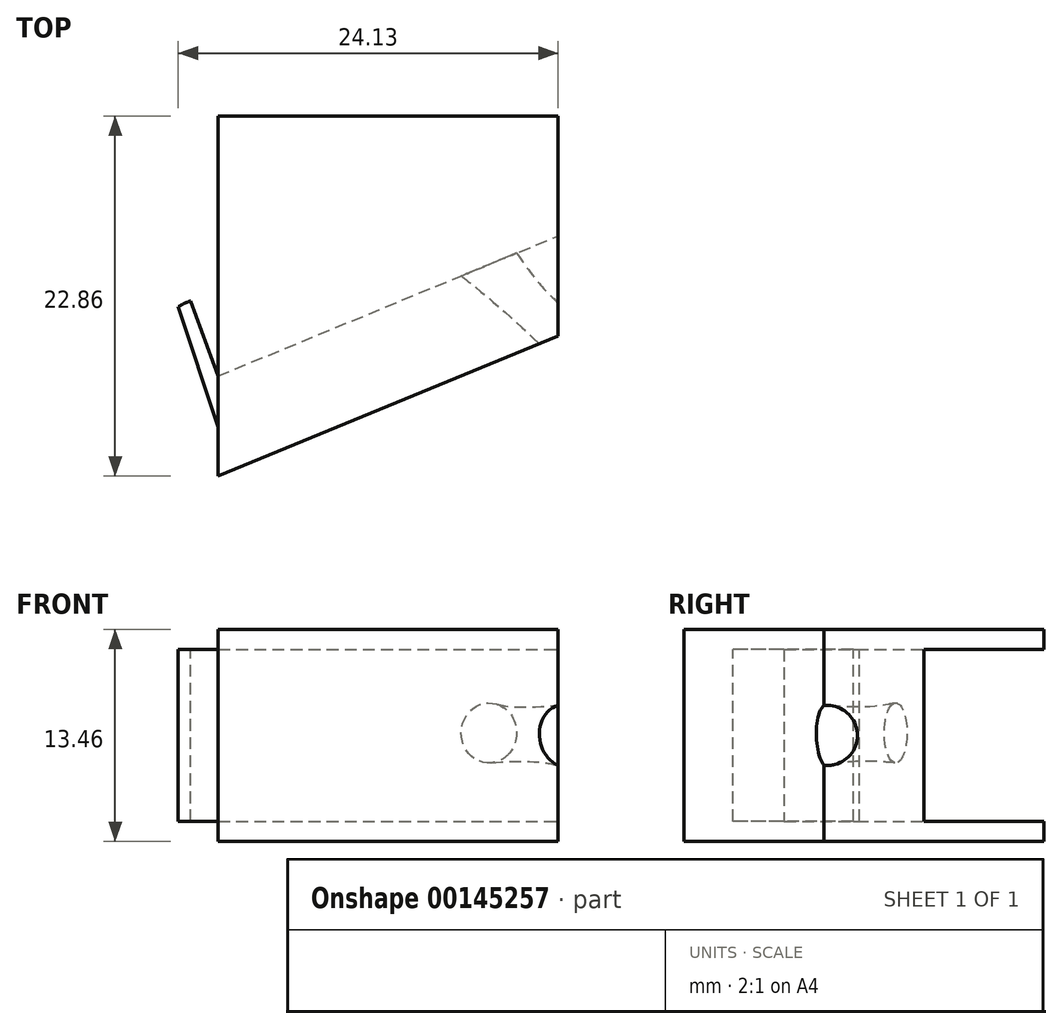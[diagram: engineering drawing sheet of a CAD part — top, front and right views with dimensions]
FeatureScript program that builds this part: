
annotation { "Feature Type Name" : "Feature", "Feature Type Description" : "" }
export const myFeature = defineFeature(function(context is Context, id is Id, definition is map)
    precondition{}
    {
        {
            var Q0;
            Q0=qCreatedBy(makeId("Top.planeOp"),FACE);
            var sketch = newSketch(context, id + "F0", { "sketchPlane" : qUnion([Q0])});
            skLineSegment(sketch, "E0.top", {"start": v(1.27, 3.85) * mm, "end": v(12.07, 3.85) * mm});
            skLineSegment(sketch, "E0.right", {"start": v(12.07, -0.48) * mm, "end": v(12.07, 3.85) * mm});
            skLineSegment(sketch, "E1.top", {"start": v(12.07, -2.5) * mm, "end": v(-9.52, -2.5) * mm});
            skLineSegment(sketch, "E1.left", {"start": v(12.07, 3.85) * mm, "end": v(12.07, -2.5) * mm});
            skLineSegment(sketch, "E1.right", {"start": v(-9.52, 3.85) * mm, "end": v(-9.52, -2.5) * mm});
            skLineSegment(sketch, "E2", {"start": v(-9.52, 3.85) * mm, "end": v(1.27, 3.85) * mm});
            skLineSegment(sketch, "E3", {"start": v(-9.52, 3.85) * mm, "end": v(12.06, 12.74) * mm});
            skLineSegment(sketch, "E4", {"start": v(12.07, 12.74) * mm, "end": v(12.07, 3.85) * mm});
            skLineSegment(sketch, "E5", {"start": v(-9.52, -2.5) * mm, "end": v(12.07, 6.4) * mm});
            skLineSegment(sketch, "E6.top", {"start": v(12.07, 20.36) * mm, "end": v(-9.52, 20.36) * mm});
            skLineSegment(sketch, "E6.left", {"start": v(12.07, -2.5) * mm, "end": v(12.07, 20.36) * mm});
            skLineSegment(sketch, "E6.right", {"start": v(-9.52, -2.5) * mm, "end": v(-9.52, 20.36) * mm});
            skSolve(sketch);
        }
        {
            var Q0;
            {var subQ6=sQuery(id+"F0.wireOp",EDGE,"E2");Q0=makeQuery(id+"F0.imprint","IMPRINT",FACE,{"disambiguationData":[TD([[makeQuery(id+"F0.imprint","IMPRINT",EDGE,{"derivedFrom":subQ6}),1.0]])]});}
            var Q1;
            {var subQ0=sQuery(id+"F0.wireOp",EDGE,"E6.left");var subQ1=sQuery(id+"F0.wireOp",EDGE,"E0.top");var subQ2=makeQuery(id+"F0.imprint","INTERSECT",VERTEX,{"derivedFrom":[subQ1,subQ0]});Q1=makeQuery(id+"F0.imprint","IMPRINT",FACE,{"disambiguationData":[TD([[makeQuery(id+"F0.imprint","IMPRINT",EDGE,{"disambiguationData":[TD([[subQ2,1.0]])],"derivedFrom":subQ1}),1.0]])]});}
            var Q2;
            {var subQ5=sQuery(id+"F0.wireOp",EDGE,"E1.top");Q2=makeQuery(id+"F0.imprint","IMPRINT",FACE,{"disambiguationData":[TD([[makeQuery(id+"F0.imprint","IMPRINT",EDGE,{"derivedFrom":subQ5}),-1.0]])]});}
            var Q3;
            {var subQ0=sQuery(id+"F0.wireOp",EDGE,"E2");Q3=makeQuery(id+"F0.imprint","IMPRINT",FACE,{"disambiguationData":[TD([[makeQuery(id+"F0.imprint","IMPRINT",EDGE,{"derivedFrom":subQ0}),-1.0]])]});}
            extrude(context, id + "F1", {"entities" : qUnion([Q0, Q1, Q2, Q3]), "depth" : 13.46 * mm});
        }
        {
            var Q0;
            Q0=makeQuery(id+"F1.opExtrude","CAP_FACE",FACE,{"disambiguationData":[OSD([sQuery(id+"F0.wireOp",EDGE,"E1.top"),sQuery(id+"F0.wireOp",EDGE,"E1.left"),sQuery(id+"F0.wireOp",EDGE,"E1.right"),sQuery(id+"F0.wireOp",EDGE,"E3"),sQuery(id+"F0.wireOp",EDGE,"E4")])],"isStart":false});
            var sketch = newSketch(context, id + "F2", { "sketchPlane" : qUnion([Q0])});
            skLineSegment(sketch, "E7.bottom", {"start": v(-9.53, -2.5) * mm, "end": v(12.07, -2.5) * mm});
            skLineSegment(sketch, "E7.top", {"start": v(-9.53, 20.36) * mm, "end": v(12.07, 20.36) * mm});
            skLineSegment(sketch, "E7.left", {"start": v(-9.53, -2.5) * mm, "end": v(-9.53, 20.36) * mm});
            skLineSegment(sketch, "E7.right", {"start": v(12.07, -2.5) * mm, "end": v(12.07, 20.36) * mm});
            skSolve(sketch);
        }
        {
            var Q0;
            {var subQ0=sQuery(id+"F2.wireOp",EDGE,"E7.top");Q0=makeQuery(id+"F2.imprint","IMPRINT",FACE,{"disambiguationData":[TD([[makeQuery(id+"F2.imprint","IMPRINT",EDGE,{"derivedFrom":subQ0}),-1.0]])]});}
            extrude(context, id + "F3", {"entities" : qUnion([Q0]), "operationType" : NewBodyOperationType.ADD, "oppositeDirection" : true, "depth" : 1.27 * mm});
        }
        {
            var Q0;
            {var subQ0=sQuery(id+"F0.wireOp",EDGE,"E3");Q0=makeQuery(id+"F0.imprint","IMPRINT",FACE,{"disambiguationData":[TD([[makeQuery(id+"F0.imprint","IMPRINT",EDGE,{"derivedFrom":subQ0}),1.0]])]});}
            extrude(context, id + "F4", {"entities" : qUnion([Q0]), "operationType" : NewBodyOperationType.ADD, "depth" : 1.27 * mm});
        }
        {
            var Q0;
            {var subQ0=sQuery(id+"F0.wireOp",EDGE,"E6.right");Q0=makeQuery(id+"F4.boolean.opBoolean","MERGE",FACE,{"derivedFrom":[makeQuery(id+"F3.boolean.opBoolean","MERGE",FACE,{"derivedFrom":[makeQuery(id+"F1.opExtrude","SWEPT_FACE",FACE,{"disambiguationData":[OSD([subQ0])]}),makeQuery(id+"F3.opExtrude","SWEPT_FACE",FACE,{"disambiguationData":[OSD([sQuery(id+"F2.wireOp",EDGE,"E7.left")])]})]}),makeQuery(id+"F4.opExtrude","SWEPT_FACE",FACE,{"disambiguationData":[OSD([subQ0])]})]});}
            var sketch = newSketch(context, id + "F5", { "sketchPlane" : qUnion([Q0])});
            skPoint(sketch, "E8.oppositeSnap0", {"position": v(-8.93, 13.46) * mm});
            skLineSegment(sketch, "E8.bottom", {"start": v(-3.85, 1.27) * mm, "end": v(-8.93, 1.27) * mm});
            skLineSegment(sketch, "E8.top", {"start": v(-3.85, 12.2) * mm, "end": v(-8.93, 12.2) * mm});
            skLineSegment(sketch, "E8.left", {"start": v(-3.85, 1.27) * mm, "end": v(-3.85, 12.2) * mm});
            skLineSegment(sketch, "E8.right", {"start": v(-8.93, 1.27) * mm, "end": v(-8.93, 12.2) * mm});
            skLineSegment(sketch, "E9.bottom", {"start": v(-2.45, 1.27) * mm, "end": v(-0.6, 1.27) * mm});
            skLineSegment(sketch, "E9.top", {"start": v(-2.45, 12.2) * mm, "end": v(-0.6, 12.2) * mm});
            skLineSegment(sketch, "E9.left", {"start": v(-2.45, 1.27) * mm, "end": v(-2.45, 12.2) * mm});
            skLineSegment(sketch, "E9.right", {"start": v(-0.6, 1.27) * mm, "end": v(-0.6, 12.2) * mm});
            skSolve(sketch);
        }
        {
            var Q0;
            Q0=makeQuery(id+"F5.imprint","IMPRINT",FACE,{"disambiguationData":[TD([[makeQuery(id+"F5.imprint","IMPRINT",EDGE,{"derivedFrom":sQuery(id+"F5.wireOp",EDGE,"E8.bottom")}),-1.0]])]});
            var Q1;
            Q1=sQuery(id+"F5.wireOp",EDGE,"E8.left");
            revolve(context, id + "F6", {"entities" : qUnion([Q0]), "axis" : qUnion([Q1]), "revolveType" : RevolveType.ONE_DIRECTION, "angle" : 30 * degree});
        }
        {
            var Q0;
            Q0=makeQuery(id+"F5.imprint","IMPRINT",FACE,{"disambiguationData":[TD([[makeQuery(id+"F5.imprint","IMPRINT",EDGE,{"derivedFrom":sQuery(id+"F5.wireOp",EDGE,"E8.bottom")}),-1.0]])]});
            var Q1;
            Q1=sQuery(id+"F5.wireOp",EDGE,"E8.left");
            revolve(context, id + "F7", {"operationType" : NewBodyOperationType.REMOVE, "entities" : qUnion([Q0]), "axis" : qUnion([Q1]), "revolveType" : RevolveType.ONE_DIRECTION, "angle" : 20 * degree});
        }
        {
            var Q0;
            Q0=makeQuery(id+"F6.opRevolve","CAP_FACE",FACE,{"disambiguationData":[OSD([sQuery(id+"F5.wireOp",EDGE,"E8.bottom"),sQuery(id+"F5.wireOp",EDGE,"E8.top"),sQuery(id+"F5.wireOp",EDGE,"E8.left"),sQuery(id+"F5.wireOp",EDGE,"E8.right")])],"isStart":false});
            var Q1;
            Q1=makeQuery(id+"F5.imprint","IMPRINT",FACE,{"disambiguationData":[TD([[makeQuery(id+"F5.imprint","IMPRINT",EDGE,{"derivedFrom":sQuery(id+"F5.wireOp",EDGE,"E9.bottom")}),1.0]])]});
            loft(context, id + "F8", {"operationType" : NewBodyOperationType.ADD, "sheetProfilesArray" : [{ "sheetProfileEntities" : qUnion([Q0]) }, { "sheetProfileEntities" : qUnion([Q1]) }]});
        }
        {
            var Q0;
            Q0=makeQuery(id+"F1.opExtrude","SWEPT_FACE",FACE,{"disambiguationData":[OSD([sQuery(id+"F0.wireOp",EDGE,"E3")])]});
            var sketch = newSketch(context, id + "F9", { "sketchPlane" : qUnion([Q0])});
            skCircle(sketch, "E10", {"center": v(-11.26, 6.89) * mm, "radius": 1.9 * mm});
            skSolve(sketch);
        }
        {
            var Q0;
            {var subQ0=sQuery(id+"F0.wireOp",EDGE,"E6.left");Q0=makeQuery(id+"F4.boolean.opBoolean","MERGE",FACE,{"derivedFrom":[makeQuery(id+"F3.boolean.opBoolean","MERGE",FACE,{"derivedFrom":[makeQuery(id+"F1.opExtrude","SWEPT_FACE",FACE,{"disambiguationData":[OSD([subQ0])]}),makeQuery(id+"F3.opExtrude","SWEPT_FACE",FACE,{"disambiguationData":[OSD([sQuery(id+"F2.wireOp",EDGE,"E7.right")])]})]}),makeQuery(id+"F4.opExtrude","SWEPT_FACE",FACE,{"disambiguationData":[OSD([subQ0])]})]});}
            var sketch = newSketch(context, id + "F10", { "sketchPlane" : qUnion([Q0])});
            skCircle(sketch, "E11", {"center": v(6.6, 6.73) * mm, "radius": 1.9 * mm});
            skSolve(sketch);
        }
        {
            var Q1;
            Q1=makeQuery(id+"F10.imprint","IMPRINT",FACE,{"disambiguationData":[TD([[makeQuery(id+"F10.imprint","IMPRINT",EDGE,{"derivedFrom":sQuery(id+"F10.wireOp",EDGE,"E11")}),1.0]])]});
            var Q2;
            Q2=makeQuery(id+"F9.imprint","IMPRINT",FACE,{"disambiguationData":[TD([[makeQuery(id+"F9.imprint","IMPRINT",EDGE,{"derivedFrom":sQuery(id+"F9.wireOp",EDGE,"E10")}),1.0]])]});
            loft(context, id + "F11", {"operationType" : NewBodyOperationType.REMOVE, "sheetProfilesArray" : [{ "sheetProfileEntities" : qUnion([Q1]) }, { "sheetProfileEntities" : qUnion([Q2]) }]});
        }
    });
